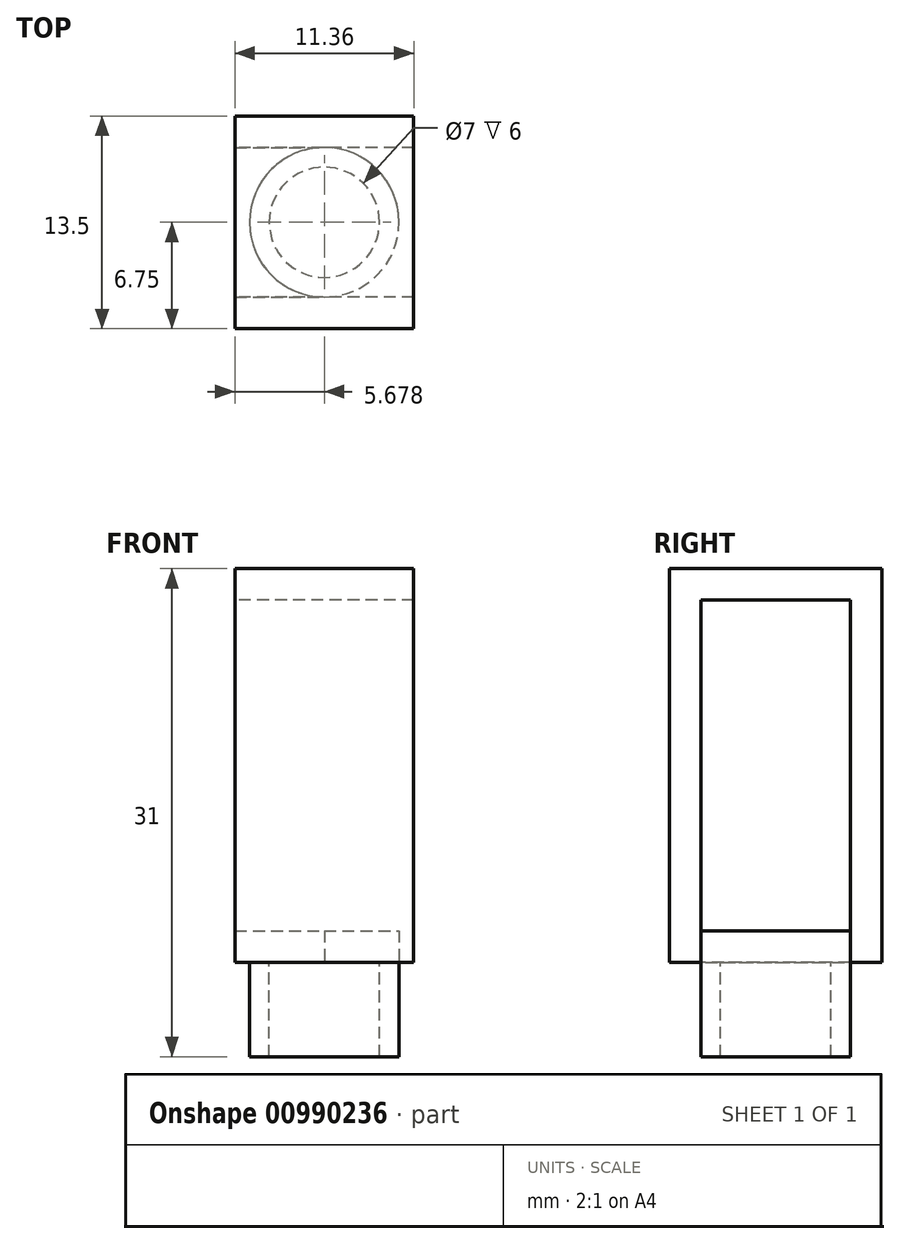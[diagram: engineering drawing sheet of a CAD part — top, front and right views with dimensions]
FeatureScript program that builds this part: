
annotation { "Feature Type Name" : "Feature", "Feature Type Description" : "" }
export const myFeature = defineFeature(function(context is Context, id is Id, definition is map)
    precondition{}
    {
        {
            var Q0;
            Q0=qCreatedBy(makeId("Top.planeOp"),FACE);
            var sketch = newSketch(context, id + "F0", { "sketchPlane" : qUnion([Q0])});
            skLineSegment(sketch, "E0.bottom", {"start": v(16, -4.75) * mm, "end": v(-16, -4.75) * mm});
            skLineSegment(sketch, "E0.top", {"start": v(16, 4.75) * mm, "end": v(-16, 4.75) * mm});
            skLineSegment(sketch, "E0.left", {"start": v(16, -4.75) * mm, "end": v(16, 4.75) * mm});
            skLineSegment(sketch, "E0.right", {"start": v(-16, -4.75) * mm, "end": v(-16, 4.75) * mm});
            skPoint(sketch, "E0.middle", {"position": v(0, 0) * mm});
            skLineSegment(sketch, "E1.bottom", {"start": v(-16, 4.75) * mm, "end": v(16, 4.75) * mm});
            skLineSegment(sketch, "E1.top", {"start": v(-16, 6.75) * mm, "end": v(16, 6.75) * mm});
            skLineSegment(sketch, "E1.left", {"start": v(-16, 4.75) * mm, "end": v(-16, 6.75) * mm});
            skLineSegment(sketch, "E1.right", {"start": v(16, 4.75) * mm, "end": v(16, 6.75) * mm});
            skLineSegment(sketch, "E2.bottom", {"start": v(-16, -4.75) * mm, "end": v(16, -4.75) * mm});
            skLineSegment(sketch, "E2.top", {"start": v(-16, -6.75) * mm, "end": v(16, -6.75) * mm});
            skLineSegment(sketch, "E2.left", {"start": v(-16, -4.75) * mm, "end": v(-16, -6.75) * mm});
            skLineSegment(sketch, "E2.right", {"start": v(16, -4.75) * mm, "end": v(16, -6.75) * mm});
            skLineSegment(sketch, "E3", {"start": v(-4.64, -6.75) * mm, "end": v(-4.64, 6.75) * mm});
            skLineSegment(sketch, "E4", {"start": v(-16, 4.75) * mm, "end": v(-4.64, -4.75) * mm, "construction": true});
            skCircle(sketch, "E5", {"center": v(-10.32, 0) * mm, "radius": 4.75 * mm});
            skCircle(sketch, "E6", {"center": v(-10.32, 0) * mm, "radius": 3.5 * mm});
            skSolve(sketch);
        }
        {
            var Q0;
            {var subQ0=sQuery(id+"F0.wireOp",EDGE,"E0.right");Q0=makeQuery(id+"F0.imprint","IMPRINT",FACE,{"disambiguationData":[TD([[makeQuery(id+"F0.imprint","IMPRINT",EDGE,{"derivedFrom":subQ0}),-1.0]])]});}
            var Q1;
            {var subQ0=sQuery(id+"F0.wireOp",EDGE,"E1.left");Q1=makeQuery(id+"F0.imprint","IMPRINT",FACE,{"disambiguationData":[TD([[makeQuery(id+"F0.imprint","IMPRINT",EDGE,{"derivedFrom":subQ0}),-1.0]])]});}
            var Q2;
            {var subQ0=sQuery(id+"F0.wireOp",EDGE,"E2.left");Q2=makeQuery(id+"F0.imprint","IMPRINT",FACE,{"disambiguationData":[TD([[makeQuery(id+"F0.imprint","IMPRINT",EDGE,{"derivedFrom":subQ0}),1.0]])]});}
            var Q3;
            {var subQ0=sQuery(id+"F0.wireOp",EDGE,"E5");var subQ1=sQuery(id+"F0.wireOp",EDGE,"E1.bottom");var subQ2=makeQuery(id+"F0.imprint","INTERSECT",VERTEX,{"derivedFrom":[subQ1,subQ0]});Q3=makeQuery(id+"F0.imprint","IMPRINT",FACE,{"disambiguationData":[TD([[makeQuery(id+"F0.imprint","IMPRINT",EDGE,{"disambiguationData":[TD([[subQ2,-1.0]])],"derivedFrom":subQ1}),-1.0]])]});}
            var Q4;
            Q4=makeQuery(id+"F0.imprint","IMPRINT",FACE,{"disambiguationData":[TD([[makeQuery(id+"F0.imprint","IMPRINT",EDGE,{"derivedFrom":sQuery(id+"F0.wireOp",EDGE,"E6")}),-1.0]])]});
            var Q5;
            Q5=makeQuery(id+"F0.imprint","IMPRINT",FACE,{"disambiguationData":[TD([[makeQuery(id+"F0.imprint","IMPRINT",EDGE,{"derivedFrom":sQuery(id+"F0.wireOp",EDGE,"E6")}),1.0]])]});
            extrude(context, id + "F1", {"entities" : qUnion([Q0, Q1, Q2, Q3, Q4, Q5]), "depth" : 2 * mm, "offsetDistance" : 25 * mm});
        }
        {
            var Q0;
            {var subQ0=sQuery(id+"F0.wireOp",EDGE,"E1.left");Q0=makeQuery(id+"F0.imprint","IMPRINT",FACE,{"disambiguationData":[TD([[makeQuery(id+"F0.imprint","IMPRINT",EDGE,{"derivedFrom":subQ0}),-1.0]])]});}
            var Q1;
            {var subQ0=sQuery(id+"F0.wireOp",EDGE,"E2.left");Q1=makeQuery(id+"F0.imprint","IMPRINT",FACE,{"disambiguationData":[TD([[makeQuery(id+"F0.imprint","IMPRINT",EDGE,{"derivedFrom":subQ0}),1.0]])]});}
            extrude(context, id + "F2", {"entities" : qUnion([Q0, Q1]), "operationType" : NewBodyOperationType.ADD, "depth" : 23 * mm, "offsetDistance" : 25 * mm});
        }
        {
            var Q0;
            Q0=makeQuery(id+"F2.opExtrude","CAP_FACE",FACE,{"disambiguationData":[OSD([sQuery(id+"F0.wireOp",EDGE,"E1.bottom"),sQuery(id+"F0.wireOp",EDGE,"E1.top"),sQuery(id+"F0.wireOp",EDGE,"E1.left"),sQuery(id+"F0.wireOp",EDGE,"E1.right")])],"isStart":false});
            var sketch = newSketch(context, id + "F3", { "sketchPlane" : qUnion([Q0])});
            skPoint(sketch, "E7.0", {"position": v(-16, 6.75) * mm});
            skPoint(sketch, "E8.0", {"position": v(-4.64, -6.75) * mm});
            skLineSegment(sketch, "E9.bottom", {"start": v(-16, 6.75) * mm, "end": v(-4.64, 6.75) * mm});
            skLineSegment(sketch, "E9.top", {"start": v(-16, -6.75) * mm, "end": v(-4.64, -6.75) * mm});
            skLineSegment(sketch, "E9.left", {"start": v(-16, 6.75) * mm, "end": v(-16, -6.75) * mm});
            skLineSegment(sketch, "E9.right", {"start": v(-4.64, 6.75) * mm, "end": v(-4.64, -6.75) * mm});
            skSolve(sketch);
        }
        {
            var Q0;
            Q0=qSketchRegion(id+"F3",true);
            extrude(context, id + "F4", {"entities" : qUnion([Q0]), "operationType" : NewBodyOperationType.ADD, "depth" : 2 * mm, "offsetDistance" : 25 * mm});
        }
        {
            var Q0;
            Q0=makeQuery(id+"F0.imprint","IMPRINT",FACE,{"disambiguationData":[TD([[makeQuery(id+"F0.imprint","IMPRINT",EDGE,{"derivedFrom":sQuery(id+"F0.wireOp",EDGE,"E6")}),-1.0]])]});
            extrude(context, id + "F5", {"entities" : qUnion([Q0]), "operationType" : NewBodyOperationType.ADD, "oppositeDirection" : true, "depth" : 6 * mm, "offsetDistance" : 25 * mm});
        }
    });
